# Revit family: ExiLED M ST LED (skrått 45 grader ned mot høyre_takmontasje)
name_source: partatom
category: Lighting Fixtures
revit_build: Autodesk Revit 2013 (Build: 20130531_2115(x64)
units: mm (PartAtom-declared; Revit-internal decimal feet)

## types (3) — shared parameters
Apparent Load = 17 VA
Body Material and Colour = Default
Color Filter = 16777215
Dimming Lamp Color Temperature Shift = <None>
Emit Shape Visible in Rendering = No
Emit from Rectangle Width = 10 mm  [stored 0.0328084 ft]
Lamp = 1
Number of Poles = 1
Photometric Web File = 20x42A12.ies
Tilt Angle = 90.00°
Voltage = 230 V
Wattage Comments = 17 W
Width = 10 mm  [stored 0.0328084 ft]
Width Top = 53 mm  [stored 0.173885 ft]

## per-type parameters (varying)
| type | 22m | 34m | 44m | Emit from Rectangle Length | Height | Height 1 | Length |
| 22m | Yes | No | No | 265 mm | 222 mm | 132 mm | 265 mm |
| 34 m | No | Yes | No | 365 mm | 272 mm | 182 mm | 365 mm |
| 44m | No | No | Yes | 455 mm | 322 mm  [stored 1.05643 ft] | 232 mm  [stored 0.761155 ft] | 455 mm |

note: [stored X ft] marks values corroborated as IEEE doubles in the binary element streams (Revit-internal decimal feet)

## geometry (parser evidence)
native form markers: Blend x2, Sweep x7
no freeform markers — native parametric forms only
